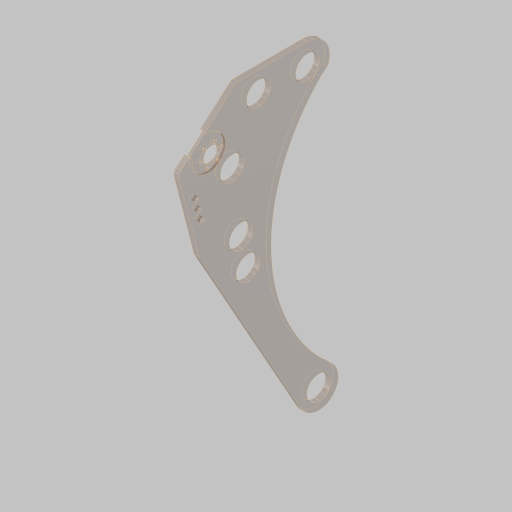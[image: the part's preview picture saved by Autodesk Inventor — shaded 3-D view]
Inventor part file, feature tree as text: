
AUTODESK INVENTOR PART (.ipt)
format: ipt  version: 2023.5 (Build 275446000, 446)  size: 287,232 bytes
history: native  units: in
note: dims shown in document units (in); Inventor stores cm internally (conversion verified against a paired STEP export)
features: sketch x8, projected_geometry x6, extrude x5, hole x2, fillet x1
ambient origin geometry x8: Origin, YZ Plane, XZ Plane, XY Plane, X Axis, Y Axis, Z Axis, Center Point
bodies: Body1 (feature_tree)
feature tree (22):
  sketch  "Sketch1"  dims[d0=16.0in d1=3.0in]
  extrude  "Extrusion2"  Depth=3.0in
  hole  "Hole2"  [1 undecoded]
  extrude  "Extrusion3"  Depth=7.0in
  fillet  "Fillet1"  Radius=1.125in
  extrude  "Extrusion4"  Depth=0.375in
  extrude  "Extrusion6"  Depth=3.75in
  hole  "Hole5"  [1 undecoded]
  extrude  "Extrusion7"  Depth=1.0in
  sketch  "Sketch4"  dims[d2=0.25in d4=4.5in]
  sketch  "Sketch5"  dims[d5=11.875in d6=7.0in d27=1.125in]
  sketch  "Sketch6"  dims[d29=0.375in d31=4.0in]
  projected_geometry  "Projected Loop1"
  sketch  "Sketch8"  dims[d33=4.0in d35=3.75in]
  sketch  "Sketch11"  dims[d36=0.25in d37=0.0in d39=0.5in]
  sketch  "Sketch12"  dims[d41=0.201in d42=0.75in d43=0.385in d44=0.25in d45=0.5635in d46=1.0in d47=0.8108in d51=6.5in]
  sketch  "Sketch13"  dims[d52=11.0in d53=1.2075in d57=1.0in d58=11.75in d59=12.75in d60=1.25in d63=1.0in d64=0.0in d65=0.5in d66=0.26in d76=0.602in d77=1.5in d78=2.256in d79=4.7708in d81=1.0in d83=0.75in d84=1.125in d85=6.2598in d87=1.5in d88=7.4409in d90=1.0in d91=0.0in d111=1.25in d112=1.6in d113=1.0in d114=0.125in d115=0.0in d116=1.0in d117=0.75in d118=2.3622in d120=360.0deg d122=0.201in d123=0.75in d124=0.385in d125=0.25in d126=0.5635in d127=1.0in d128=0.8108in d133=1.125in d134=1.87in d135=2.815in d136=0.125in d137=0.0in d138=0.5in d139=2.4in d142=2.7514in d143=2.402in d144=2.25in]
  projected_geometry  "Project Cut Edges1"
  projected_geometry  "Project Cut Edges4"
  projected_geometry  "Project Cut Edges5"
  projected_geometry  "Project Cut Edges6"
  projected_geometry  "Project Cut Edges7"
note: 2 required parameter values undecoded (feature->parameter linkage not recoverable at this tier; creation-order binding heuristic only, values carry confidence <= 0.55)
